# Revit family: Gira_5032219
name_source: partatom
category: Elektroinstallationen
revit_build: Autodesk Revit 2017 (Build: 20160225_1515(x64)
units: mm (PartAtom-declared; Revit-internal decimal feet)

## family parameters
Basisbauteil = Fläche
Beim Laden mit Abzugskörper schneiden = Nein
Bemaßung runder Anschluss = Durchmesser verwenden
Beschriftungsausrichtung beibehalten = Nein
Gemeinsam genutzt = Nein
Raumberechnungspunkt = Nein
Teiletyp = Normal

## types (1)
- Wippenset 2f indiv. Tastsens.4 TS4 Edelstahl
    Andere Bussysteme = ohne
    BIM = https://media.stage.bim.site TS4 Wippenset 2fach.rfa
    BIMSITE_PRODUCT_ID = 1a05b85d3f3910ac22999a805da374a53793c4d7
    Beschreibung = Wippenset 2fach individuell für Tastsensor 4  Edelstahl Hinweise :  Beschreibbare Wippensets können mit einer individuellen Beschriftung versehen werden. Die Bestellung wird über den Großhandel abgewickelt, der beim Bestellvorgang der Wippen angegeben wurde.  Dieses Produkt kann ausschließlich über den Gira Beschriftungsservice bestellt werden.  Professionelle Beschriftung über den Gira Beschriftungsservice www.beschriftung.gira.de.
    Bussystem Funkbus = Nein
    Bussystem KNX = Ja
    Bussystem KNX-Funk = Nein
    Bussystem LON = Nein
    Bussystem Powernet = Nein
    Datenblatt = https://media.stage.bim.site
    Datenblatt 1 = https://media.stage.bim.site
    Farbe = Edelstahl
    Funk bidirektional = Nein
    GTIN = 4010337072591
    HAN = 5032219
    HeinzeBIM = https://www.heinze.de
    Hersteller = Gira
    Kosten = 0 $
    Produktseite = https://media.stage.bim.site
    Transparent = Nein
    Typname = Wippenset 2f indiv. Tastsens.4 TS4 Edelstahl
    URL = https://www.gira.de
    Vorgabe-Ansicht = 1219 mm
    Werkstoff Text = Metall
    Werkstoffgüte = Edelstahl

## geometry (parser evidence)
native form markers: Sweep x4
no freeform markers — native parametric forms only
